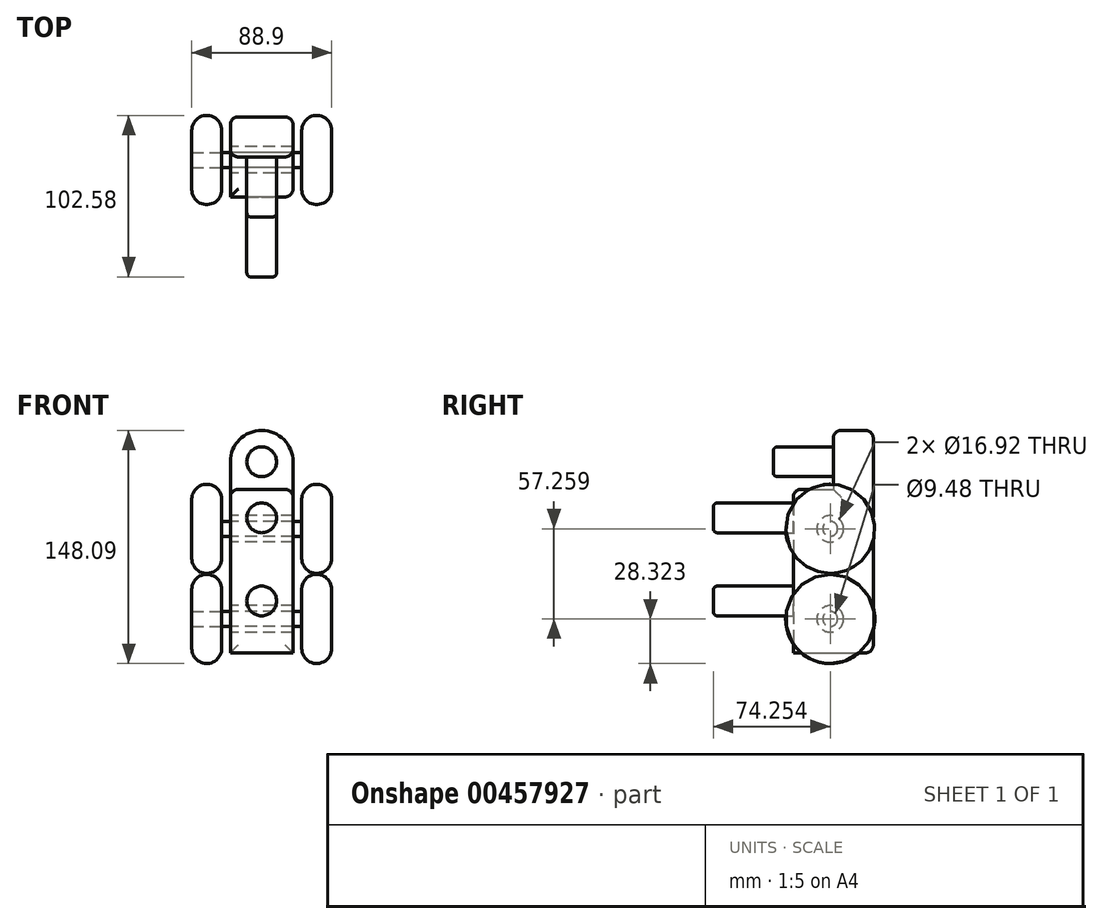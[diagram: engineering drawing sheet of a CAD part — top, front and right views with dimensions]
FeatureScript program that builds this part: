
annotation { "Feature Type Name" : "Feature", "Feature Type Description" : "" }
export const myFeature = defineFeature(function(context is Context, id is Id, definition is map)
    precondition{}
    {
        {
            var Q0;
            Q0=qCreatedBy(makeId("Front.planeOp"),FACE);
            var sketch = newSketch(context, id + "F0", { "sketchPlane" : qUnion([Q0])});
            skArc(sketch, "E0", {"start": v(19.93, 0) * mm, "mid": v(0, 19.93) * mm, "end": v(-19.93, 0) * mm});
            skLineSegment(sketch, "E1", {"start": v(-19.93, 0) * mm, "end": v(-19.93, -121.45) * mm});
            skLineSegment(sketch, "E2", {"start": v(19.93, 0) * mm, "end": v(19.93, -121.45) * mm});
            skArc(sketch, "E3", {"start": v(19.93, -121.45) * mm, "mid": v(0, -141.38) * mm, "end": v(-19.93, -121.45) * mm});
            skLineSegment(sketch, "E4", {"start": v(19.93, -121.45) * mm, "end": v(-19.93, -121.45) * mm});
            skLineSegment(sketch, "E5", {"start": v(19.93, -17.52) * mm, "end": v(-19.93, -17.52) * mm});
            skCircle(sketch, "E6", {"center": v(0, 0) * mm, "radius": 9.46 * mm});
            skCircle(sketch, "E7", {"center": v(0, -35.64) * mm, "radius": 9.46 * mm});
            skPoint(sketch, "E7.centerSnap0", {"position": v(0, -17.52) * mm});
            skCircle(sketch, "E8", {"center": v(0, -88.4) * mm, "radius": 9.46 * mm});
            skSolve(sketch);
        }
        {
            var Q0;
            Q0=makeQuery(id+"F0.imprint","IMPRINT",FACE,{"disambiguationData":[TD([[makeQuery(id+"F0.imprint","IMPRINT",EDGE,{"derivedFrom":sQuery(id+"F0.wireOp",EDGE,"E7")}),1.0]])]});
            var Q1;
            Q1=makeQuery(id+"F0.imprint","IMPRINT",FACE,{"disambiguationData":[TD([[makeQuery(id+"F0.imprint","IMPRINT",EDGE,{"derivedFrom":sQuery(id+"F0.wireOp",EDGE,"E8")}),1.0]])]});
            extrude(context, id + "F1", {"entities" : qUnion([Q0, Q1]), "depth" : 101.6 * mm, "offsetDistance" : 25.4 * mm});
        }
        {
            var Q0;
            {var subQ0=sQuery(id+"F0.wireOp",EDGE,"E4");Q0=makeQuery(id+"F0.imprint","IMPRINT",FACE,{"disambiguationData":[TD([[makeQuery(id+"F0.imprint","IMPRINT",EDGE,{"derivedFrom":subQ0}),-1.0]])]});}
            var Q1;
            Q1=makeQuery(id+"F0.imprint","IMPRINT",FACE,{"disambiguationData":[TD([[makeQuery(id+"F0.imprint","IMPRINT",EDGE,{"derivedFrom":sQuery(id+"F0.wireOp",EDGE,"E3")}),-1.0]])]});
            extrude(context, id + "F2", {"entities" : qUnion([Q0, Q1]), "operationType" : NewBodyOperationType.ADD, "depth" : 50.8 * mm, "offsetDistance" : 25.4 * mm});
        }
        {
            var Q0;
            {var subQ2=sQuery(id+"F0.wireOp",EDGE,"E0");Q0=makeQuery(id+"F0.imprint","IMPRINT",FACE,{"disambiguationData":[TD([[makeQuery(id+"F0.imprint","IMPRINT",EDGE,{"derivedFrom":subQ2}),1.0]])]});}
            extrude(context, id + "F3", {"entities" : qUnion([Q0]), "operationType" : NewBodyOperationType.ADD, "depth" : 25.4 * mm, "offsetDistance" : 25.4 * mm});
        }
        {
            var Q0;
            Q0=makeQuery(id+"F0.imprint","IMPRINT",FACE,{"disambiguationData":[TD([[makeQuery(id+"F0.imprint","IMPRINT",EDGE,{"derivedFrom":sQuery(id+"F0.wireOp",EDGE,"E6")}),1.0]])]});
            extrude(context, id + "F4", {"entities" : qUnion([Q0]), "operationType" : NewBodyOperationType.ADD, "depth" : 63.5 * mm, "offsetDistance" : 25.4 * mm});
        }
        {
            var Q0;
            Q0=makeQuery(id+"F2.opExtrude","SWEPT_EDGE",EDGE,{"disambiguationData":[OSD([sQuery(id+"F0.wireOp",EDGE,"E1"),sQuery(id+"F0.wireOp",EDGE,"E5")])]});
            var Q1;
            Q1=makeQuery(id+"F2.opExtrude","CAP_EDGE",EDGE,{"disambiguationData":[OSD([sQuery(id+"F0.wireOp",EDGE,"E2")])],"isStart":false});
            var Q2;
            Q2=makeQuery(id+"F2.opExtrude","CAP_EDGE",EDGE,{"disambiguationData":[OSD([sQuery(id+"F0.wireOp",EDGE,"E5")])],"isStart":false});
            var Q3;
            Q3=makeQuery(id+"F2.opExtrude","SWEPT_EDGE",EDGE,{"disambiguationData":[OSD([sQuery(id+"F0.wireOp",EDGE,"E2"),sQuery(id+"F0.wireOp",EDGE,"E5")])]});
            fillet(context, id + "F5", {"entities" : qUnion([Q0, Q1, Q2, Q3]), "radius" : 5.08 * mm, "tangentPropagation" : true, "allowEdgeOverflow" : false});
        }
        {
            var Q0;
            {var subQ0=sQuery(id+"F0.wireOp",EDGE,"E6");var subQ1=sQuery(id+"F0.wireOp",EDGE,"E5");var subQ2=sQuery(id+"F0.wireOp",EDGE,"E2");var subQ3=sQuery(id+"F0.wireOp",EDGE,"E1");var subQ4=sQuery(id+"F0.wireOp",EDGE,"E8");var subQ5=sQuery(id+"F0.wireOp",EDGE,"E7");Q0=makeQuery(id+"F4.boolean.opBoolean","MERGE",FACE,{"derivedFrom":[makeQuery(id+"F3.boolean.opBoolean","MERGE",FACE,{"derivedFrom":[makeQuery(id+"F2.boolean.opBoolean","MERGE",FACE,{"derivedFrom":[makeQuery(id+"F1.opExtrude","CAP_FACE",FACE,{"disambiguationData":[OSD([subQ5])],"isStart":true}),makeQuery(id+"F1.opExtrude","CAP_FACE",FACE,{"disambiguationData":[OSD([subQ4])],"isStart":true}),makeQuery(id+"F2.opExtrude","CAP_FACE",FACE,{"disambiguationData":[OSD([subQ3,subQ2,sQuery(id+"F0.wireOp",EDGE,"E3"),subQ1,subQ5,subQ4])],"isStart":true})]}),makeQuery(id+"F3.opExtrude","CAP_FACE",FACE,{"disambiguationData":[OSD([sQuery(id+"F0.wireOp",EDGE,"E0"),subQ3,subQ2,subQ1,subQ0])],"isStart":true})]}),makeQuery(id+"F4.opExtrude","CAP_FACE",FACE,{"disambiguationData":[OSD([subQ0])],"isStart":true})]});}
            fillet(context, id + "F6", {"entities" : qUnion([Q0]), "radius" : 5.08 * mm, "tangentPropagation" : true, "allowEdgeOverflow" : false});
        }
        {
            var Q0;
            Q0=makeQuery(id+"F3.opExtrude","CAP_EDGE",EDGE,{"disambiguationData":[OSD([sQuery(id+"F0.wireOp",EDGE,"E1")])],"isStart":false});
            var Q1;
            Q1=makeQuery(id+"F3.opExtrude","CAP_EDGE",EDGE,{"disambiguationData":[OSD([sQuery(id+"F0.wireOp",EDGE,"E0")])],"isStart":false});
            var Q2;
            Q2=makeQuery(id+"F3.opExtrude","SWEPT_EDGE",EDGE,{"disambiguationData":[OSD([sQuery(id+"F0.wireOp",EDGE,"E0"),sQuery(id+"F0.wireOp",EDGE,"E2")])]});
            fillet(context, id + "F7", {"entities" : qUnion([Q0, Q1, Q2]), "radius" : 5.08 * mm, "tangentPropagation" : true, "allowEdgeOverflow" : false});
        }
        {
            var Q0;
            Q0=qCreatedBy(makeId("Right.planeOp"),FACE);
            var sketch = newSketch(context, id + "F8", { "sketchPlane" : qUnion([Q0])});
            skCircle(sketch, "E9", {"center": v(-27.35, -42.58) * mm, "radius": 8.46 * mm});
            skCircle(sketch, "E10", {"center": v(-27.35, -99.84) * mm, "radius": 8.46 * mm});
            skSolve(sketch);
        }
        {
            var Q0;
            Q0=qSketchRegion(id+"F8",true);
            extrude(context, id + "F9", {"entities" : qUnion([Q0]), "operationType" : NewBodyOperationType.REMOVE, "endBound" : BoundingType.SYMMETRIC, "depth" : 50.8 * mm, "offsetDistance" : 25.4 * mm});
        }
        {
            var Q0;
            Q0=qCreatedBy(makeId("Right.planeOp"),FACE);
            var sketch = newSketch(context, id + "F10", { "sketchPlane" : qUnion([Q0])});
            skCircle(sketch, "E11.0", {"center": v(-27.35, -42.58) * mm, "radius": 4.74 * mm});
            skCircle(sketch, "E12.0", {"center": v(-27.35, -42.58) * mm, "radius": 8.46 * mm});
            skCircle(sketch, "E13.0", {"center": v(-27.35, -99.84) * mm, "radius": 8.46 * mm});
            skCircle(sketch, "E14", {"center": v(-27.35, -99.84) * mm, "radius": 4.74 * mm});
            skSolve(sketch);
        }
        {
            var Q0;
            Q0=makeQuery(id+"F10.imprint","IMPRINT",FACE,{"disambiguationData":[TD([[makeQuery(id+"F10.imprint","IMPRINT",EDGE,{"derivedFrom":sQuery(id+"F10.wireOp",EDGE,"E11.0")}),1.0]])]});
            var Q1;
            Q1=makeQuery(id+"F10.imprint","IMPRINT",FACE,{"disambiguationData":[TD([[makeQuery(id+"F10.imprint","IMPRINT",EDGE,{"derivedFrom":sQuery(id+"F10.wireOp",EDGE,"E14")}),1.0]])]});
            var Q2;
            Q2=sQuery(id+"F10.wireOp",EDGE,"E11.0");
            var Q3;
            Q3=sQuery(id+"F10.wireOp",EDGE,"E14");
            extrude(context, id + "F11", {"entities" : qUnion([Q0, Q1]), "surfaceEntities" : qUnion([Q2, Q3]), "endBound" : BoundingType.SYMMETRIC, "depth" : 50.8 * mm, "offsetDistance" : 25.4 * mm});
        }
        {
            var Q0;
            Q0=makeQuery(id+"F1.opExtrude","CAP_EDGE",EDGE,{"disambiguationData":[OSD([sQuery(id+"F0.wireOp",EDGE,"E8")])],"isStart":false});
            var Q1;
            Q1=makeQuery(id+"F1.opExtrude","CAP_EDGE",EDGE,{"disambiguationData":[OSD([sQuery(id+"F0.wireOp",EDGE,"E7")])],"isStart":false});
            var Q2;
            Q2=makeQuery(id+"F4.opExtrude","CAP_EDGE",EDGE,{"disambiguationData":[OSD([sQuery(id+"F0.wireOp",EDGE,"E6")])],"isStart":false});
            fillet(context, id + "F12", {"entities" : qUnion([Q0, Q1, Q2]), "radius" : 2.54 * mm, "tangentPropagation" : true, "allowEdgeOverflow" : false});
        }
        {
            var Q0;
            Q0=qCreatedBy(makeId("Right.planeOp"),FACE);
            var sketch = newSketch(context, id + "F13", { "sketchPlane" : qUnion([Q0])});
            skCircle(sketch, "E15", {"center": v(-27.35, -99.84) * mm, "radius": 15.5 * mm});
            skCircle(sketch, "E16", {"center": v(-27.35, -42.58) * mm, "radius": 15.5 * mm});
            skCircle(sketch, "E17.0", {"center": v(-27.35, -42.58) * mm, "radius": 4.74 * mm});
            skCircle(sketch, "E18.0", {"center": v(-27.35, -99.84) * mm, "radius": 4.74 * mm});
            skSolve(sketch);
        }
        {
            var Q0;
            Q0=makeQuery(id+"F11.opExtrude","CAP_FACE",FACE,{"disambiguationData":[OSD([sQuery(id+"F10.wireOp",EDGE,"E11.0")])],"isStart":false});
            var sketch = newSketch(context, id + "F14", { "sketchPlane" : qUnion([Q0])});
            skCircle(sketch, "E19.0", {"center": v(-27.35, -42.58) * mm, "radius": 4.74 * mm});
            skCircle(sketch, "E20.0", {"center": v(-27.35, -99.84) * mm, "radius": 4.74 * mm});
            skCircle(sketch, "E21", {"center": v(-27.35, -42.58) * mm, "radius": 28.32 * mm});
            skCircle(sketch, "E22", {"center": v(-27.35, -99.84) * mm, "radius": 28.32 * mm});
            skSolve(sketch);
        }
        {
            var Q0;
            Q0 = qSketchRegion(id + "F14", true);
            var Q1;
            Q1=makeQuery(id+"F14.imprint","IMPRINT",FACE,{"disambiguationData":[TD([[makeQuery(id+"F14.imprint","IMPRINT",EDGE,{"derivedFrom":sQuery(id+"F14.wireOp",EDGE,"E19.0")}),1.0]])]});
            var Q2;
            Q2=makeQuery(id+"F14.imprint","IMPRINT",FACE,{"disambiguationData":[TD([[makeQuery(id+"F14.imprint","IMPRINT",EDGE,{"derivedFrom":sQuery(id+"F14.wireOp",EDGE,"E20.0")}),1.0]])]});
            extrude(context, id + "F15", {"entities" : qUnion([Q0, Q1, Q2]), "depth" : 19.05 * mm, "offsetDistance" : 25.4 * mm});
        }
        {
            var Q0;
            Q0=makeQuery(id+"F15.opExtrude","CAP_EDGE",EDGE,{"disambiguationData":[OSD([sQuery(id+"F14.wireOp",EDGE,"E21")])],"isStart":false});
            var Q1;
            Q1=makeQuery(id+"F15.opExtrude","CAP_EDGE",EDGE,{"disambiguationData":[OSD([sQuery(id+"F14.wireOp",EDGE,"E22")])],"isStart":false});
            var Q2;
            Q2=makeQuery(id+"F15.opExtrude","CAP_EDGE",EDGE,{"disambiguationData":[OSD([sQuery(id+"F14.wireOp",EDGE,"E22")])],"isStart":true});
            var Q3;
            Q3=makeQuery(id+"F15.opExtrude","CAP_EDGE",EDGE,{"disambiguationData":[OSD([sQuery(id+"F14.wireOp",EDGE,"E21")])],"isStart":true});
            fillet(context, id + "F16", {"entities" : qUnion([Q0, Q1, Q2, Q3]), "radius" : 9.52 * mm, "tangentPropagation" : true, "allowEdgeOverflow" : false});
        }
        {
            var Q0;
            Q0=makeQuery(id+"F11.opExtrude","CAP_FACE",FACE,{"disambiguationData":[OSD([sQuery(id+"F10.wireOp",EDGE,"E11.0")])],"isStart":true});
            var sketch = newSketch(context, id + "F17", { "sketchPlane" : qUnion([Q0])});
            skCircle(sketch, "E23.0", {"center": v(27.35, -42.58) * mm, "radius": 4.74 * mm});
            skCircle(sketch, "E24.0", {"center": v(27.35, -99.84) * mm, "radius": 4.74 * mm});
            skCircle(sketch, "E25", {"center": v(27.35, -42.58) * mm, "radius": 28.32 * mm});
            skCircle(sketch, "E26", {"center": v(27.35, -99.84) * mm, "radius": 28.32 * mm});
            skSolve(sketch);
        }
        {
            var Q0;
            Q0 = qSketchRegion(id + "F17", true);
            var Q1;
            Q1=makeQuery(id+"F17.imprint","IMPRINT",FACE,{"disambiguationData":[TD([[makeQuery(id+"F17.imprint","IMPRINT",EDGE,{"derivedFrom":sQuery(id+"F17.wireOp",EDGE,"E23.0")}),-1.0]])]});
            var Q2;
            Q2=makeQuery(id+"F17.imprint","IMPRINT",FACE,{"disambiguationData":[TD([[makeQuery(id+"F17.imprint","IMPRINT",EDGE,{"derivedFrom":sQuery(id+"F17.wireOp",EDGE,"E24.0")}),-1.0]])]});
            extrude(context, id + "F18", {"entities" : qUnion([Q0, Q1, Q2]), "depth" : 19.05 * mm, "offsetDistance" : 25.4 * mm});
        }
        {
            var Q0;
            Q0=makeQuery(id+"F18.opExtrude","CAP_EDGE",EDGE,{"disambiguationData":[OSD([sQuery(id+"F17.wireOp",EDGE,"E25")])],"isStart":false});
            var Q1;
            Q1=makeQuery(id+"F18.opExtrude","CAP_EDGE",EDGE,{"disambiguationData":[OSD([sQuery(id+"F17.wireOp",EDGE,"E25")])],"isStart":true});
            var Q2;
            Q2=makeQuery(id+"F18.opExtrude","CAP_EDGE",EDGE,{"disambiguationData":[OSD([sQuery(id+"F17.wireOp",EDGE,"E26")])],"isStart":false});
            var Q3;
            Q3=makeQuery(id+"F18.opExtrude","CAP_EDGE",EDGE,{"disambiguationData":[OSD([sQuery(id+"F17.wireOp",EDGE,"E26")])],"isStart":true});
            fillet(context, id + "F19", {"entities" : qUnion([Q0, Q1, Q2, Q3]), "radius" : 9.52 * mm, "tangentPropagation" : true, "allowEdgeOverflow" : false});
        }
    });
